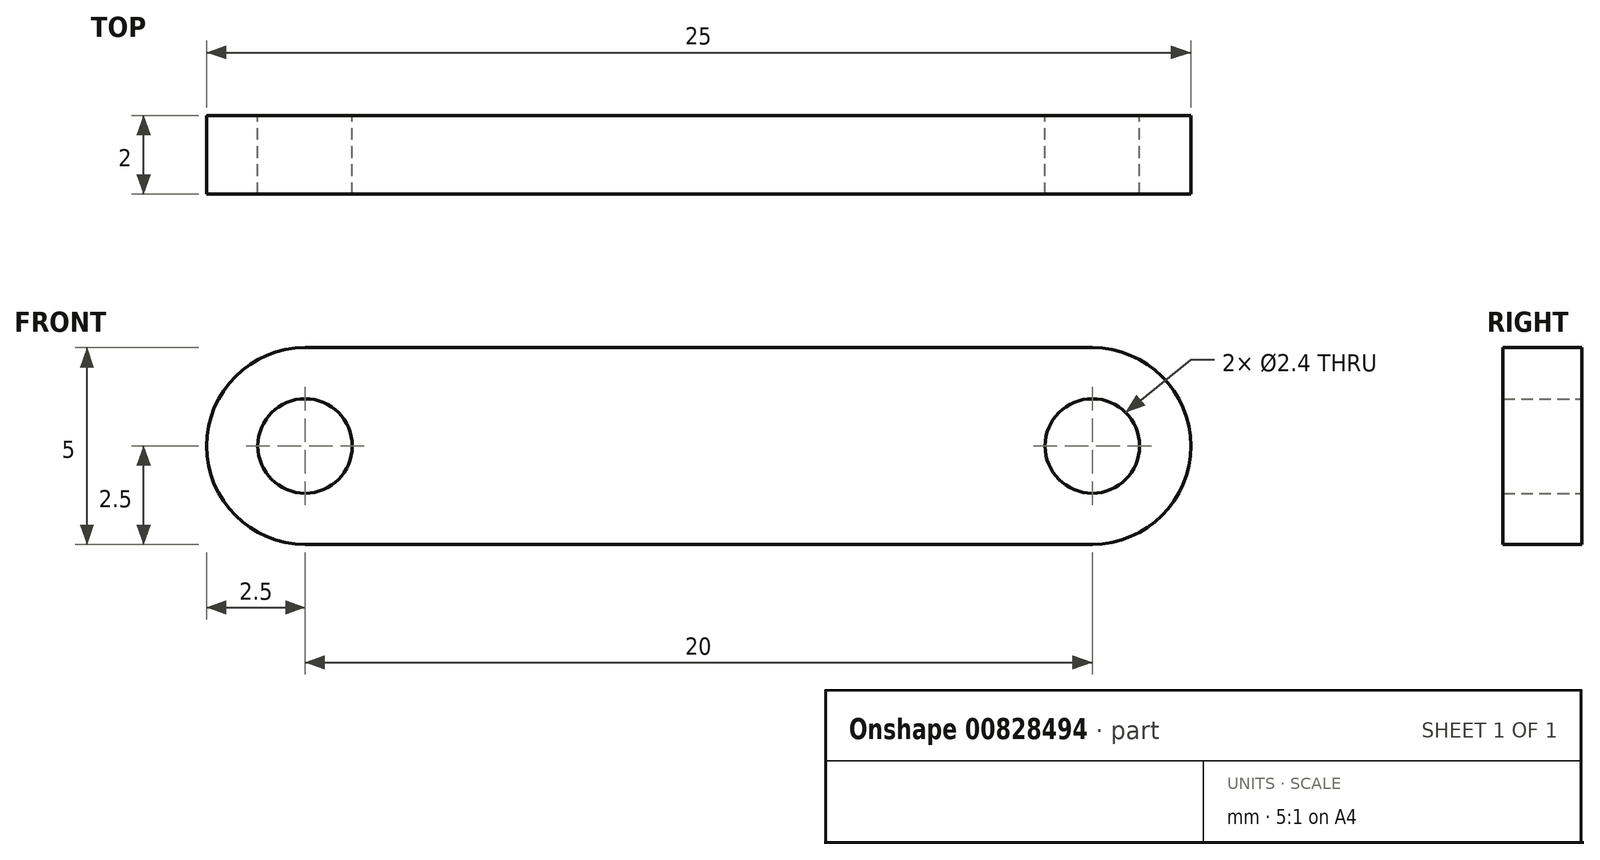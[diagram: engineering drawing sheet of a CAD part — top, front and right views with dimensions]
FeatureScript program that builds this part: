
annotation { "Feature Type Name" : "Feature", "Feature Type Description" : "" }
export const myFeature = defineFeature(function(context is Context, id is Id, definition is map)
    precondition{}
    {
        {
            var Q0;
            Q0=qCreatedBy(makeId("Front.planeOp"),FACE);
            var sketch = newSketch(context, id + "F0", { "sketchPlane" : qUnion([Q0])});
            skArc(sketch, "E0", {"start": v(-10, 2.5) * mm, "mid": v(-11.77, 1.77) * mm, "end": v(-12.5, 0) * mm});
            skLineSegment(sketch, "E1", {"start": v(0, 0) * mm, "end": v(-10, 0) * mm, "construction": true});
            skLineSegment(sketch, "E2", {"start": v(-10, 2.5) * mm, "end": v(0, 2.5) * mm});
            skLineSegment(sketch, "E3", {"start": v(0, 2.5) * mm, "end": v(0, 0) * mm, "construction": true});
            skCircle(sketch, "E4", {"center": v(-10, 0) * mm, "radius": 1.2 * mm});
            skLineSegment(sketch, "E5.MirrorCS", {"start": v(-10, -2.5) * mm, "end": v(0, -2.5) * mm});
            skArc(sketch, "E6.MirrorCS", {"start": v(-10, -2.5) * mm, "mid": v(-11.77, -1.77) * mm, "end": v(-12.5, 0) * mm});
            skLineSegment(sketch, "E7.MirrorCS", {"start": v(10, 2.5) * mm, "end": v(0, 2.5) * mm});
            skArc(sketch, "E8.MirrorCS", {"start": v(10, 2.5) * mm, "mid": v(11.77, 1.77) * mm, "end": v(12.5, 0) * mm});
            skCircle(sketch, "E9.MirrorC", {"center": v(10, 0) * mm, "radius": 1.2 * mm});
            skArc(sketch, "E10.MirrorCS", {"start": v(10, -2.5) * mm, "mid": v(11.77, -1.77) * mm, "end": v(12.5, 0) * mm});
            skLineSegment(sketch, "E11.MirrorCS", {"start": v(10, -2.5) * mm, "end": v(0, -2.5) * mm});
            skSolve(sketch);
        }
        {
            var Q0;
            Q0=makeQuery(id+"F0.imprint","IMPRINT",FACE,{"disambiguationData":[TD([[makeQuery(id+"F0.imprint","IMPRINT",EDGE,{"derivedFrom":sQuery(id+"F0.wireOp",EDGE,"E0")}),1.0]])]});
            extrude(context, id + "F1", {"entities" : qUnion([Q0]), "depth" : 2 * mm, "offsetDistance" : 25 * mm});
        }
    });
